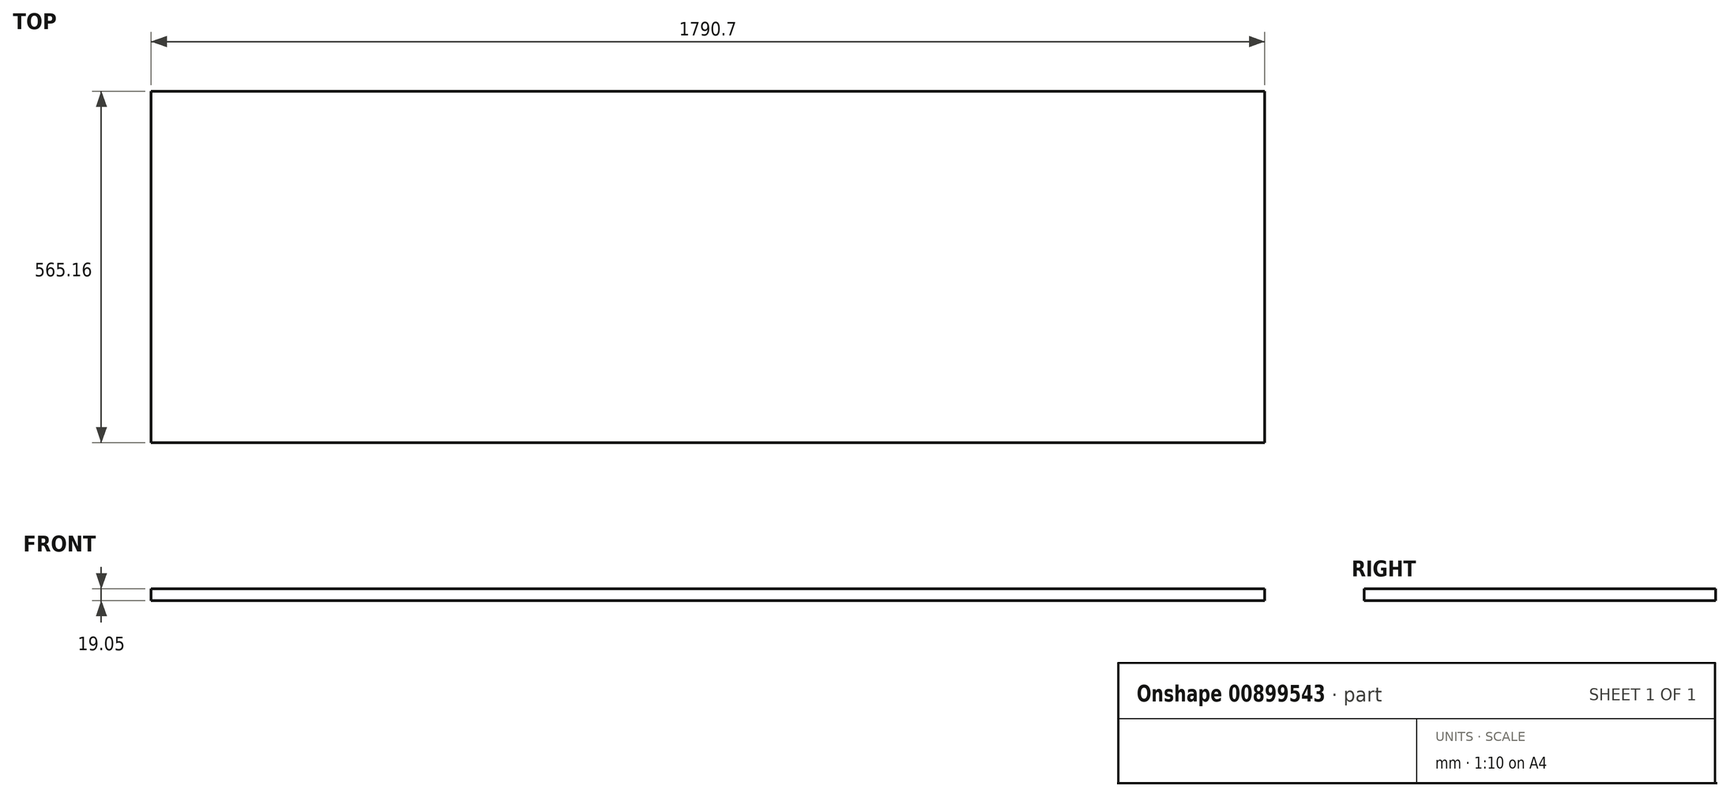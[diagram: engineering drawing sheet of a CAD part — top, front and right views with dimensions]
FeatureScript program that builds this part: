
annotation { "Feature Type Name" : "Feature", "Feature Type Description" : "" }
export const myFeature = defineFeature(function(context is Context, id is Id, definition is map)
    precondition{}
    {
        {
            var Q0;
            Q0=qCreatedBy(makeId("Top.planeOp"),FACE);
            var sketch = newSketch(context, id + "F0", { "sketchPlane" : qUnion([Q0])});
            skLineSegment(sketch, "E0.bottom", {"start": v(895.35, 282.58) * mm, "end": v(-895.35, 282.58) * mm});
            skLineSegment(sketch, "E0.top", {"start": v(895.35, -282.58) * mm, "end": v(-895.35, -282.58) * mm});
            skLineSegment(sketch, "E0.left", {"start": v(895.35, 282.58) * mm, "end": v(895.35, -282.58) * mm});
            skLineSegment(sketch, "E0.right", {"start": v(-895.35, 282.58) * mm, "end": v(-895.35, -282.58) * mm});
            skPoint(sketch, "E0.middle", {"position": v(0, 0) * mm});
            skSolve(sketch);
        }
        {
            var Q0;
            Q0=makeQuery(id+"F0.imprint","IMPRINT",FACE,{"disambiguationData":[TD([[makeQuery(id+"F0.imprint","IMPRINT",EDGE,{"derivedFrom":sQuery(id+"F0.wireOp",EDGE,"E0.bottom")}),1.0]])]});
            extrude(context, id + "F1", {"entities" : qUnion([Q0]), "depth" : 19.05 * mm, "offsetDistance" : 25.4 * mm});
        }
    });
